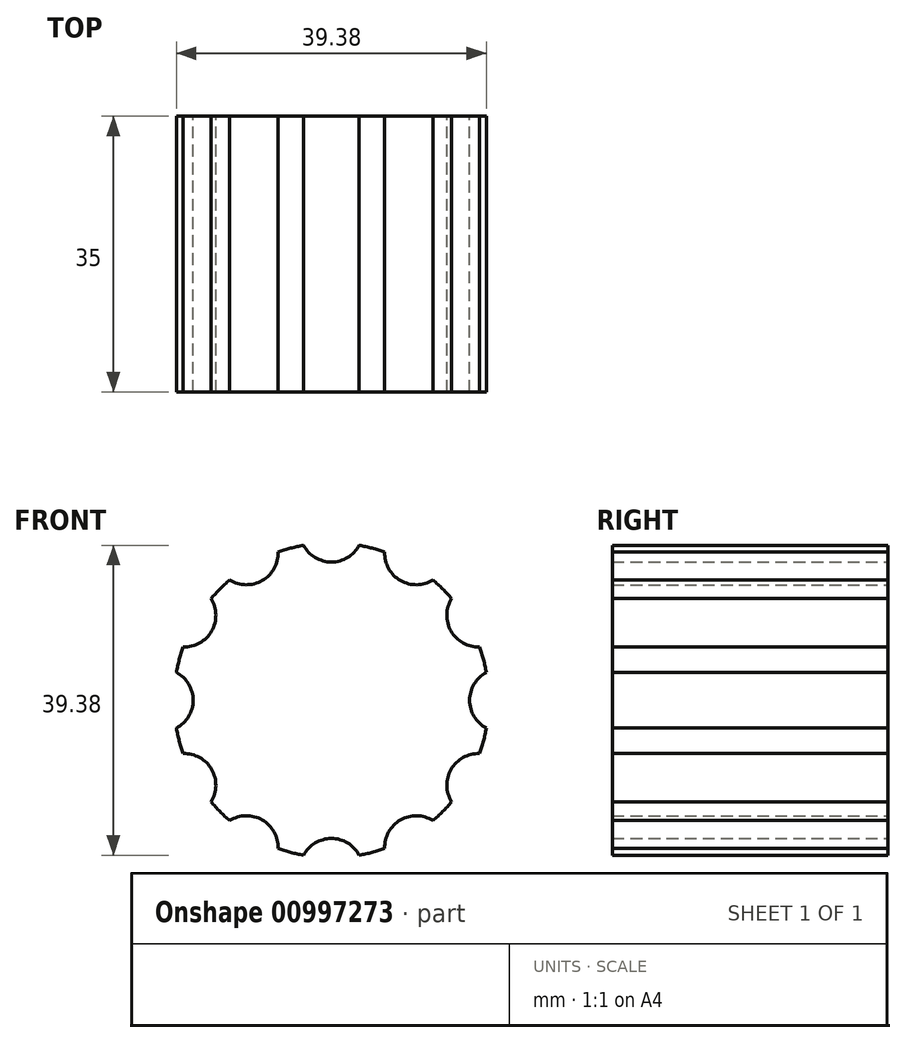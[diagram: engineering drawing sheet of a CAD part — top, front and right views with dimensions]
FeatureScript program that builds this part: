
annotation { "Feature Type Name" : "Feature", "Feature Type Description" : "" }
export const myFeature = defineFeature(function(context is Context, id is Id, definition is map)
    precondition{}
    {
        {
            var Q0;
            Q0=qCreatedBy(makeId("Front.planeOp"),FACE);
            var sketch = newSketch(context, id + "F0", { "sketchPlane" : qUnion([Q0])});
            skArc(sketch, "E0", {"start": v(-3.53, 19.69) * mm, "mid": v(0, 17.56) * mm, "end": v(3.53, 19.69) * mm});
            skArc(sketch, "E1.1.0", {"start": v(12.9, -15.28) * mm, "mid": v(14.14, -14.14) * mm, "end": v(15.28, -12.9) * mm});
            skArc(sketch, "E1.2.0", {"start": v(12.9, -15.28) * mm, "mid": v(14.14, -14.14) * mm, "end": v(15.28, -12.9) * mm, "construction": true});
            skPoint(sketch, "E1.center", {"position": v(0, 0) * mm});
            skArc(sketch, "E2.1.0", {"start": v(-12.9, 15.28) * mm, "mid": v(-8.78, 15.2) * mm, "end": v(-6.78, 18.81) * mm});
            skArc(sketch, "E2.2.0", {"start": v(-18.81, 6.78) * mm, "mid": v(-15.2, 8.78) * mm, "end": v(-15.28, 12.9) * mm});
            skArc(sketch, "E2.3.0", {"start": v(-19.69, -3.53) * mm, "mid": v(-17.56, 0) * mm, "end": v(-19.69, 3.53) * mm});
            skArc(sketch, "E2.4.0", {"start": v(-15.28, -12.9) * mm, "mid": v(-15.2, -8.78) * mm, "end": v(-18.81, -6.78) * mm});
            skArc(sketch, "E2.5.0", {"start": v(-6.78, -18.81) * mm, "mid": v(-8.78, -15.2) * mm, "end": v(-12.9, -15.28) * mm});
            skArc(sketch, "E2.6.0", {"start": v(3.53, -19.69) * mm, "mid": v(0, -17.56) * mm, "end": v(-3.53, -19.69) * mm});
            skArc(sketch, "E2.7.0", {"start": v(12.9, -15.28) * mm, "mid": v(8.78, -15.2) * mm, "end": v(6.78, -18.81) * mm});
            skArc(sketch, "E2.8.0", {"start": v(18.81, -6.78) * mm, "mid": v(15.2, -8.78) * mm, "end": v(15.28, -12.9) * mm});
            skArc(sketch, "E2.9.0", {"start": v(19.69, 3.53) * mm, "mid": v(17.56, 0) * mm, "end": v(19.69, -3.53) * mm});
            skArc(sketch, "E2.10.0", {"start": v(15.28, 12.9) * mm, "mid": v(15.2, 8.78) * mm, "end": v(18.81, 6.78) * mm});
            skArc(sketch, "E2.11.0", {"start": v(6.78, 18.81) * mm, "mid": v(8.78, 15.2) * mm, "end": v(12.9, 15.28) * mm});
            skArc(sketch, "E3.trimOffspring", {"start": v(-18.81, 6.78) * mm, "mid": v(-19.32, 5.18) * mm, "end": v(-19.69, 3.53) * mm});
            skArc(sketch, "E4.trimOffspring", {"start": v(15.28, 12.9) * mm, "mid": v(14.14, 14.14) * mm, "end": v(12.9, 15.28) * mm});
            skArc(sketch, "E5.trimOffspring", {"start": v(19.69, 3.53) * mm, "mid": v(19.32, 5.18) * mm, "end": v(18.81, 6.78) * mm});
            skArc(sketch, "E6.trimOffspring", {"start": v(18.81, -6.78) * mm, "mid": v(19.32, -5.18) * mm, "end": v(19.69, -3.53) * mm});
            skArc(sketch, "E7.trimOffspring", {"start": v(3.53, -19.69) * mm, "mid": v(5.18, -19.32) * mm, "end": v(6.78, -18.81) * mm});
            skArc(sketch, "E8.trimOffspring", {"start": v(-18.81, 6.78) * mm, "mid": v(-19.32, 5.18) * mm, "end": v(-19.69, 3.53) * mm, "construction": true});
            skArc(sketch, "E9.trimOffspring", {"start": v(-12.9, 15.28) * mm, "mid": v(-14.14, 14.14) * mm, "end": v(-15.28, 12.9) * mm, "construction": true});
            skArc(sketch, "E10.trimOffspring", {"start": v(-12.9, 15.28) * mm, "mid": v(-14.14, 14.14) * mm, "end": v(-15.28, 12.9) * mm});
            skArc(sketch, "E11.trimOffspring", {"start": v(-3.53, 19.69) * mm, "mid": v(-5.18, 19.32) * mm, "end": v(-6.78, 18.81) * mm, "construction": true});
            skArc(sketch, "E12.trimOffspring", {"start": v(-3.53, 19.69) * mm, "mid": v(-5.18, 19.32) * mm, "end": v(-6.78, 18.81) * mm});
            skArc(sketch, "E13.trimOffspring", {"start": v(6.78, 18.81) * mm, "mid": v(5.18, 19.32) * mm, "end": v(3.53, 19.69) * mm, "construction": true});
            skArc(sketch, "E14.trimOffspring", {"start": v(6.78, 18.81) * mm, "mid": v(5.18, 19.32) * mm, "end": v(3.53, 19.69) * mm});
            skArc(sketch, "E15.trimOffspring", {"start": v(15.28, 12.9) * mm, "mid": v(14.14, 14.14) * mm, "end": v(12.9, 15.28) * mm, "construction": true});
            skArc(sketch, "E16.trimOffspring", {"start": v(19.69, 3.53) * mm, "mid": v(19.32, 5.18) * mm, "end": v(18.81, 6.78) * mm, "construction": true});
            skArc(sketch, "E17.trimOffspring", {"start": v(18.81, -6.78) * mm, "mid": v(19.32, -5.18) * mm, "end": v(19.69, -3.53) * mm, "construction": true});
            skArc(sketch, "E18.trimOffspring", {"start": v(3.53, -19.69) * mm, "mid": v(5.18, -19.32) * mm, "end": v(6.78, -18.81) * mm, "construction": true});
            skArc(sketch, "E19.trimOffspring", {"start": v(-6.78, -18.81) * mm, "mid": v(-5.18, -19.32) * mm, "end": v(-3.53, -19.69) * mm, "construction": true});
            skArc(sketch, "E20.trimOffspring", {"start": v(-6.78, -18.81) * mm, "mid": v(-5.18, -19.32) * mm, "end": v(-3.53, -19.69) * mm});
            skArc(sketch, "E21.trimOffspring", {"start": v(-15.28, -12.9) * mm, "mid": v(-14.14, -14.14) * mm, "end": v(-12.9, -15.28) * mm, "construction": true});
            skArc(sketch, "E22.trimOffspring", {"start": v(-15.28, -12.9) * mm, "mid": v(-14.14, -14.14) * mm, "end": v(-12.9, -15.28) * mm});
            skArc(sketch, "E23.trimOffspring", {"start": v(-19.69, -3.53) * mm, "mid": v(-19.32, -5.18) * mm, "end": v(-18.81, -6.78) * mm, "construction": true});
            skArc(sketch, "E24.trimOffspring", {"start": v(-19.69, -3.53) * mm, "mid": v(-19.32, -5.18) * mm, "end": v(-18.81, -6.78) * mm});
            skSolve(sketch);
        }
        {
            var Q0;
            Q0 = qSketchRegion(id + "F0", true);
            extrude(context, id + "F1", {"entities" : qUnion([Q0]), "depth" : 35 * mm, "offsetDistance" : 25 * mm});
        }
    });
